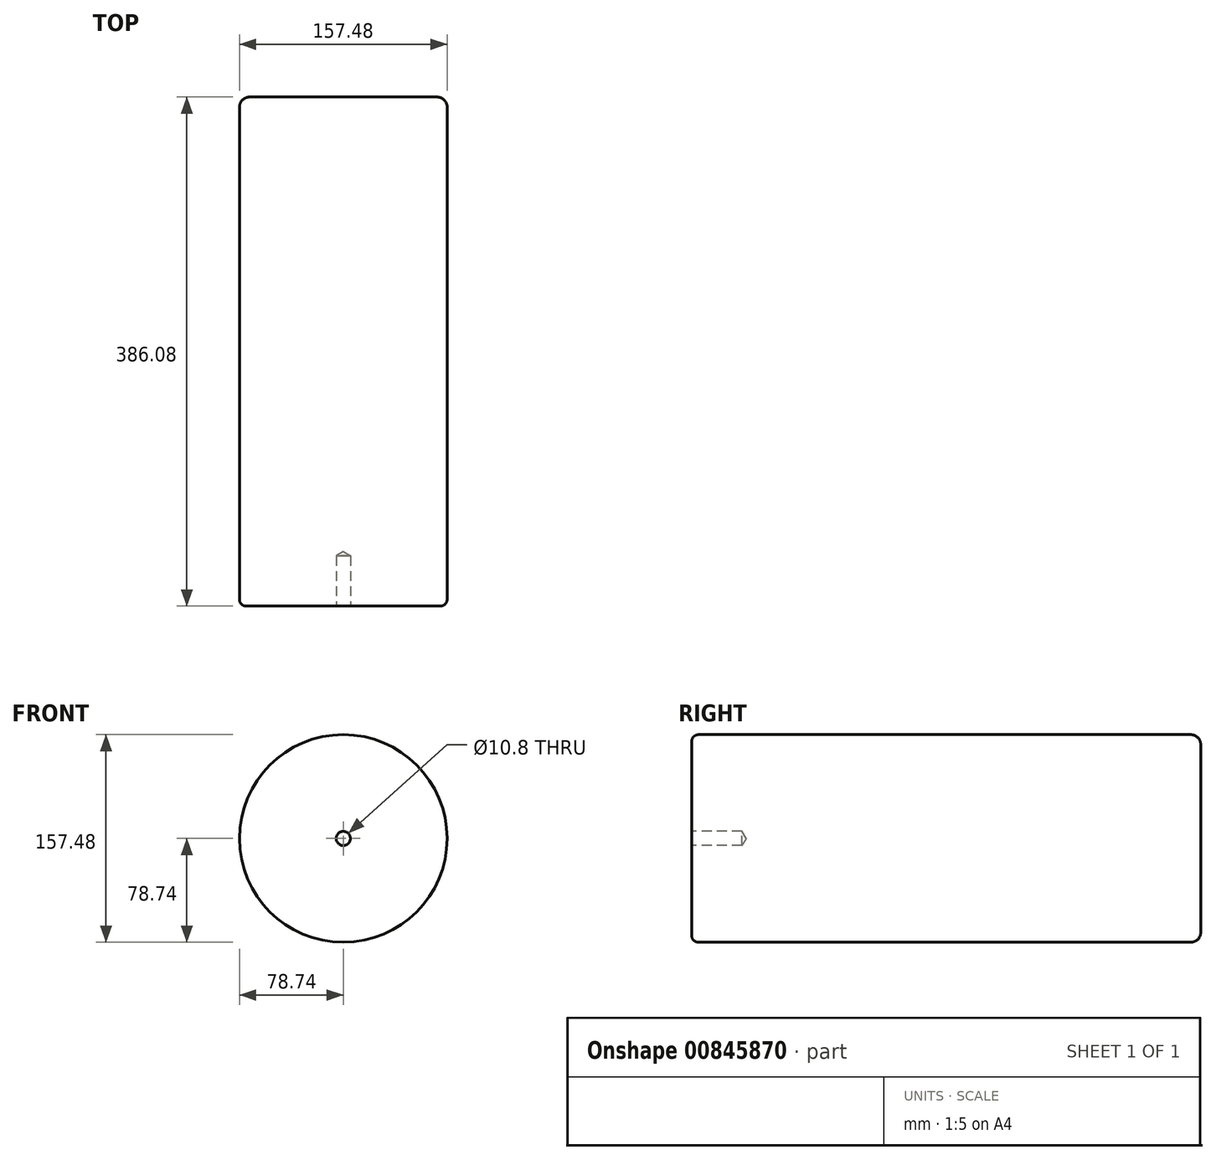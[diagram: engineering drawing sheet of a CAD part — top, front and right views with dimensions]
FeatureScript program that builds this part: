
annotation { "Feature Type Name" : "Feature", "Feature Type Description" : "" }
export const myFeature = defineFeature(function(context is Context, id is Id, definition is map)
    precondition{}
    {
        {
            var Q0;
            Q0=qCreatedBy(makeId("Front.planeOp"),FACE);
            var sketch = newSketch(context, id + "F0", { "sketchPlane" : qUnion([Q0])});
            skCircle(sketch, "E0", {"center": v(0, 0) * mm, "radius": 78.74 * mm});
            skSolve(sketch);
        }
        {
            var Q0;
            Q0=makeQuery(id+"F0.imprint","IMPRINT",FACE,{"disambiguationData":[TD([[makeQuery(id+"F0.imprint","IMPRINT",EDGE,{"derivedFrom":sQuery(id+"F0.wireOp",EDGE,"E0")}),1.0]])]});
            extrude(context, id + "F1", {"entities" : qUnion([Q0]), "depth" : 386.08 * mm, "offsetDistance" : 25.4 * mm});
        }
        {
            var Q0;
            Q0=makeQuery(id+"F1.opExtrude","CAP_FACE",FACE,{"disambiguationData":[OSD([sQuery(id+"F0.wireOp",EDGE,"E0")])],"isStart":false});
            var sketch = newSketch(context, id + "F2", { "sketchPlane" : qUnion([Q0])});
            skPoint(sketch, "E1", {"position": v(0, 0) * mm});
            skSolve(sketch);
        }
        {
            var Q0;
            Q0=sQuery(id+"F2.wireOp",VERTEX,"E1");
            var Q1;
            Q1=makeQuery(id+"F1.opExtrude","SWEPT_BODY",BODY,{"disambiguationData":[OSD([sQuery(id+"F0.wireOp",EDGE,"E0")])]});
            hole(context, id + "F3", {"style" : HoleStyle.SIMPLE, "endStyle" : HoleEndStyle.BLIND, "standardTappedOrClearance" : lookupTablePath({ "standard" : "ISO", "engagement" : "75%", "pitch" : "1.25 mm", "size" : "M12", "type" : "Tapped" }), "standardBlindInLast" : lookupTablePath({ "standard" : "ISO", "engagement" : "75%", "pitch" : "1.25 mm", "size" : "M12", "type" : "Tapped" }), "holeDiameter" : 10.8 * mm, "majorDiameter" : 12 * mm, "showTappedDepth" : true, "holeDepth" : 38.1 * mm, "isTappedThrough" : true, "tappedDepth" : 34.35 * mm, "tapClearance" : 3, "startFromSketch" : true, "locations" : qUnion([Q0]), "scope" : qUnion([Q1])});
        }
        {
            var Q0;
            Q0=makeQuery(id+"F1.opExtrude","CAP_EDGE",EDGE,{"disambiguationData":[OSD([sQuery(id+"F0.wireOp",EDGE,"E0")])],"isStart":false});
            fillet(context, id + "F4", {"entities" : qUnion([Q0]), "radius" : 5.08 * mm, "tangentPropagation" : true, "allowEdgeOverflow" : false});
        }
        {
            var Q0;
            Q0=makeQuery(id+"F1.opExtrude","CAP_EDGE",EDGE,{"disambiguationData":[OSD([sQuery(id+"F0.wireOp",EDGE,"E0")])],"isStart":true});
            fillet(context, id + "F5", {"entities" : qUnion([Q0]), "radius" : 7.62 * mm, "tangentPropagation" : true, "allowEdgeOverflow" : false});
        }
    });
